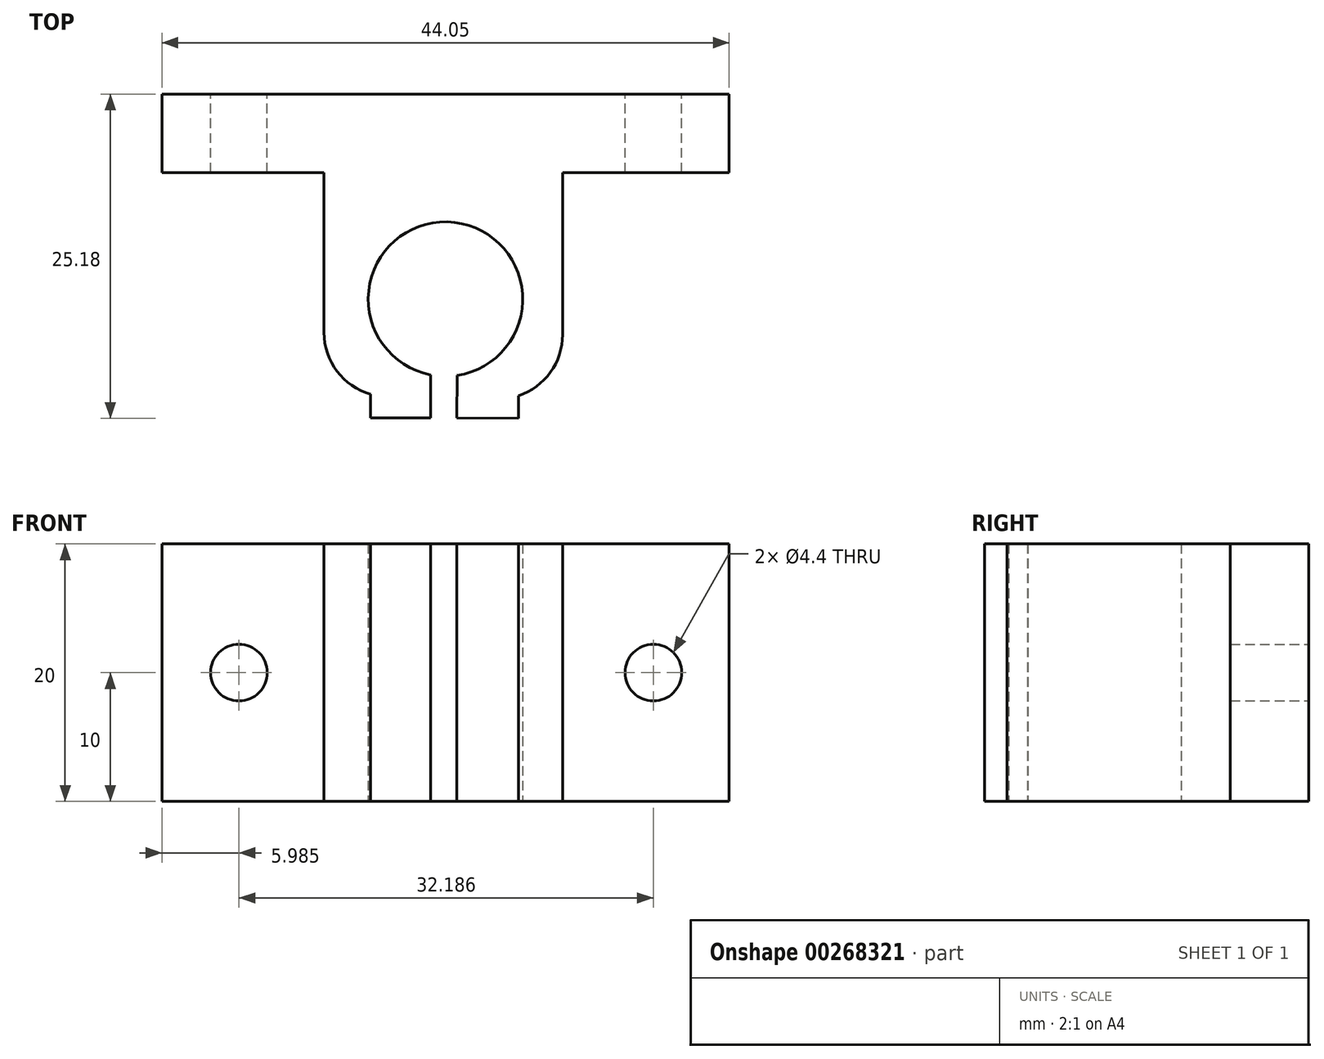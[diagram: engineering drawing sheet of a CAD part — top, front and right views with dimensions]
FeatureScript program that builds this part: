
annotation { "Feature Type Name" : "Feature", "Feature Type Description" : "" }
export const myFeature = defineFeature(function(context is Context, id is Id, definition is map)
    precondition{}
    {
        {
            var Q0;
            Q0=qCreatedBy(makeId("Top.planeOp"),FACE);
            var sketch = newSketch(context, id + "F0", { "sketchPlane" : qUnion([Q0])});
            skLineSegment(sketch, "E0", {"start": v(-25.59, 10.7) * mm, "end": v(18.46, 10.7) * mm});
            skLineSegment(sketch, "E1", {"start": v(18.46, 10.7) * mm, "end": v(18.46, 4.6) * mm});
            skLineSegment(sketch, "E2", {"start": v(18.46, 4.6) * mm, "end": v(5.54, 4.6) * mm});
            skLineSegment(sketch, "E3", {"start": v(5.54, 4.6) * mm, "end": v(5.54, -7.98) * mm});
            skLineSegment(sketch, "E4", {"start": v(-13, -7.82) * mm, "end": v(-13, 4.6) * mm});
            skLineSegment(sketch, "E5", {"start": v(-13, 4.6) * mm, "end": v(-25.59, 4.6) * mm});
            skLineSegment(sketch, "E6", {"start": v(-25.59, 4.6) * mm, "end": v(-25.59, 10.7) * mm});
            skPoint(sketch, "E7.visualSharp", {"position": v(-13, -11.73) * mm});
            skArc(sketch, "E7.filletArc", {"start": v(-13, -7.82) * mm, "mid": v(-11.99, -10.83) * mm, "end": v(-9.38, -12.63) * mm});
            skPoint(sketch, "E8.visualSharp", {"position": v(5.54, -11.73) * mm});
            skArc(sketch, "E8.filletArc", {"start": v(2.1, -12.73) * mm, "mid": v(4.59, -10.9) * mm, "end": v(5.54, -7.98) * mm});
            skArc(sketch, "E9", {"start": v(-2.67, -11.16) * mm, "mid": v(-3.43, 0.78) * mm, "end": v(-4.73, -11.1) * mm});
            skPoint(sketch, "E9.centerSnap0", {"position": v(-3.56, 10.7) * mm});
            skLineSegment(sketch, "E10", {"start": v(-9.38, -12.63) * mm, "end": v(-9.38, -14.45) * mm});
            skLineSegment(sketch, "E11", {"start": v(-9.38, -14.45) * mm, "end": v(-4.73, -14.45) * mm});
            skLineSegment(sketch, "E12", {"start": v(-4.73, -14.45) * mm, "end": v(-4.73, -11.1) * mm});
            skLineSegment(sketch, "E13", {"start": v(-2.67, -11.16) * mm, "end": v(-2.7, -14.45) * mm});
            skLineSegment(sketch, "E14", {"start": v(-2.7, -14.45) * mm, "end": v(2.1, -14.5) * mm});
            skLineSegment(sketch, "E15", {"start": v(2.1, -14.5) * mm, "end": v(2.1, -12.73) * mm});
            skSolve(sketch);
        }
        {
            var Q0;
            Q0=qSketchRegion(id+"F0",true);
            extrude(context, id + "F1", {"entities" : qUnion([Q0]), "depth" : 20 * mm});
        }
        {
            var Q0;
            Q0=makeQuery(id+"F1.opExtrude","SWEPT_FACE",FACE,{"disambiguationData":[OSD([sQuery(id+"F0.wireOp",EDGE,"E0")])]});
            var sketch = newSketch(context, id + "F2", { "sketchPlane" : qUnion([Q0])});
            skCircle(sketch, "E16", {"center": v(-12.58, 10) * mm, "radius": 2.2 * mm});
            skPoint(sketch, "E16.centerSnap0", {"position": v(-18.46, 10) * mm});
            skCircle(sketch, "E17", {"center": v(19.6, 10) * mm, "radius": 2.2 * mm});
            skPoint(sketch, "E17.centerSnap0", {"position": v(25.59, 10) * mm});
            skSolve(sketch);
        }
        {
            var Q0;
            Q0=qSketchRegion(id+"F2",true);
            extrude(context, id + "F3", {"entities" : qUnion([Q0]), "operationType" : NewBodyOperationType.REMOVE, "oppositeDirection" : true, "depth" : 25 * mm});
        }
    });
